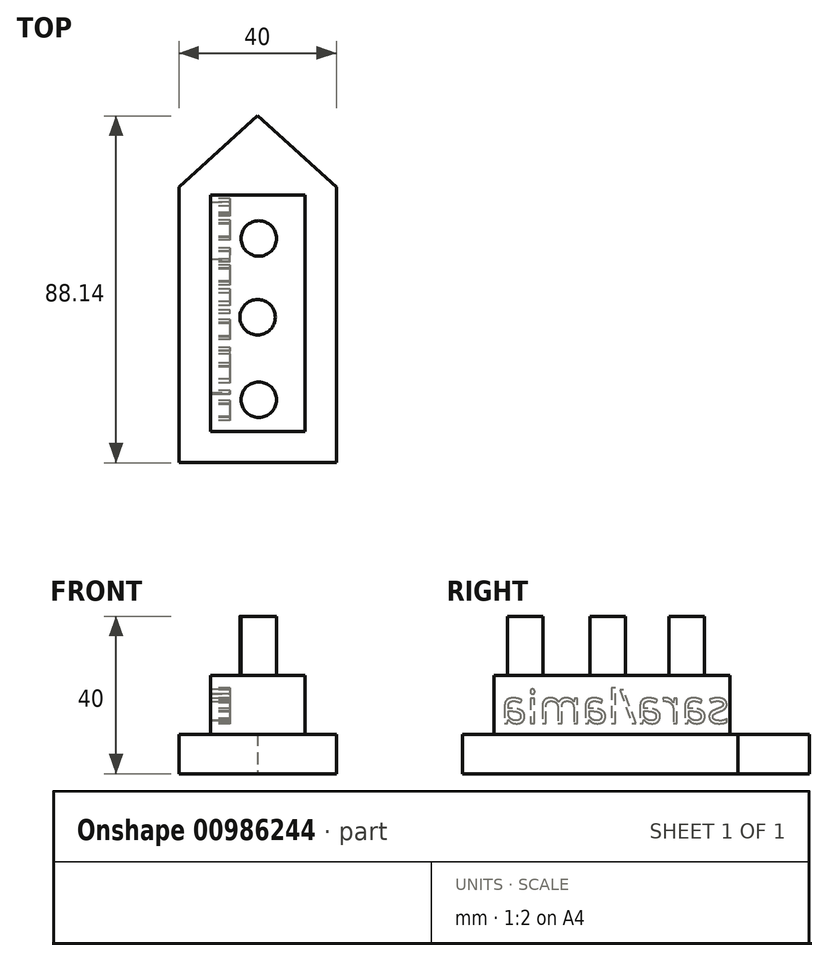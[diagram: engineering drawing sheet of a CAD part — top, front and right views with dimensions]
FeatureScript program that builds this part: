
annotation { "Feature Type Name" : "Feature", "Feature Type Description" : "" }
export const myFeature = defineFeature(function(context is Context, id is Id, definition is map)
    precondition{}
    {
        {
            var Q0;
            Q0=qCreatedBy(makeId("Top.planeOp"),FACE);
            var sketch = newSketch(context, id + "F0", { "sketchPlane" : qUnion([Q0])});
            skLineSegment(sketch, "E0", {"start": v(-20.3, 24.38) * mm, "end": v(-20.3, -45.62) * mm});
            skLineSegment(sketch, "E1", {"start": v(-20.3, -45.62) * mm, "end": v(19.7, -45.62) * mm});
            skLineSegment(sketch, "E2", {"start": v(19.7, -45.62) * mm, "end": v(19.7, 24.38) * mm});
            skLineSegment(sketch, "E3", {"start": v(-20.3, 24.38) * mm, "end": v(-0.3, 42.52) * mm});
            skLineSegment(sketch, "E4", {"start": v(-0.3, 42.52) * mm, "end": v(19.7, 24.38) * mm});
            skSolve(sketch);
        }
        {
            var Q0;
            Q0=makeQuery(id+"F0.imprint","IMPRINT",FACE,{"disambiguationData":[TD([[makeQuery(id+"F0.imprint","IMPRINT",EDGE,{"derivedFrom":sQuery(id+"F0.wireOp",EDGE,"E0")}),1.0]])]});
            extrude(context, id + "F1", {"entities" : qUnion([Q0]), "depth" : 10 * mm, "offsetDistance" : 25 * mm});
        }
        {
            var Q0;
            Q0=qCreatedBy(makeId("Top.planeOp"),FACE);
            var sketch = newSketch(context, id + "F2", { "sketchPlane" : qUnion([Q0])});
            skLineSegment(sketch, "E5.bottom", {"start": v(-12.3, 22.38) * mm, "end": v(11.7, 22.38) * mm});
            skLineSegment(sketch, "E5.top", {"start": v(-12.3, -37.62) * mm, "end": v(11.7, -37.62) * mm});
            skLineSegment(sketch, "E5.left", {"start": v(-12.3, 22.38) * mm, "end": v(-12.3, -37.62) * mm});
            skLineSegment(sketch, "E5.right", {"start": v(11.7, 22.38) * mm, "end": v(11.7, -37.62) * mm});
            skSolve(sketch);
        }
        {
            var Q0;
            Q0 = qSketchRegion(id + "F2", true);
            extrude(context, id + "F3", {"entities" : qUnion([Q0]), "operationType" : NewBodyOperationType.ADD, "depth" : 25 * mm, "offsetDistance" : 25 * mm});
        }
        {
            var Q0;
            Q0=makeQuery(id+"F3.opExtrude","CAP_FACE",FACE,{"disambiguationData":[OSD([sQuery(id+"F2.wireOp",EDGE,"E5.bottom"),sQuery(id+"F2.wireOp",EDGE,"E5.top"),sQuery(id+"F2.wireOp",EDGE,"E5.left"),sQuery(id+"F2.wireOp",EDGE,"E5.right")])],"isStart":false});
            var sketch = newSketch(context, id + "F4", { "sketchPlane" : qUnion([Q0])});
            skCircle(sketch, "E6", {"center": v(0, 11.36) * mm, "radius": 4.5 * mm});
            skCircle(sketch, "E7", {"center": v(-0.3, -8.64) * mm, "radius": 4.5 * mm});
            skCircle(sketch, "E8", {"center": v(0, -29.6) * mm, "radius": 4.5 * mm});
            skSolve(sketch);
        }
        {
            var Q0;
            Q0 = qSketchRegion(id + "F4", true);
            extrude(context, id + "F5", {"entities" : qUnion([Q0]), "operationType" : NewBodyOperationType.ADD, "depth" : 15 * mm, "offsetDistance" : 25 * mm});
        }
        {
            var Q0;
            Q0=makeQuery(id+"F3.opExtrude","SWEPT_FACE",FACE,{"disambiguationData":[OSD([sQuery(id+"F2.wireOp",EDGE,"E5.left")])]});
            var sketch = newSketch(context, id + "F6", { "sketchPlane" : qUnion([Q0])});
            skText(sketch, "E9", { "text": "sara/lamia", "fontName": "OpenSans-Regular.ttf"});
            const initialGuessF6  = {"E9": [-0.02217, 0.01282, 1, 0, 0.0085]};
            skSetInitialGuess(sketch, initialGuessF6);
            skSolve(sketch);
        }
        {
            var Q0;
            Q0 = qSketchRegion(id + "F6", true);
            extrude(context, id + "F7", {"entities" : qUnion([Q0]), "operationType" : NewBodyOperationType.REMOVE, "oppositeDirection" : true, "depth" : 5 * mm, "offsetDistance" : 25 * mm});
        }
    });
